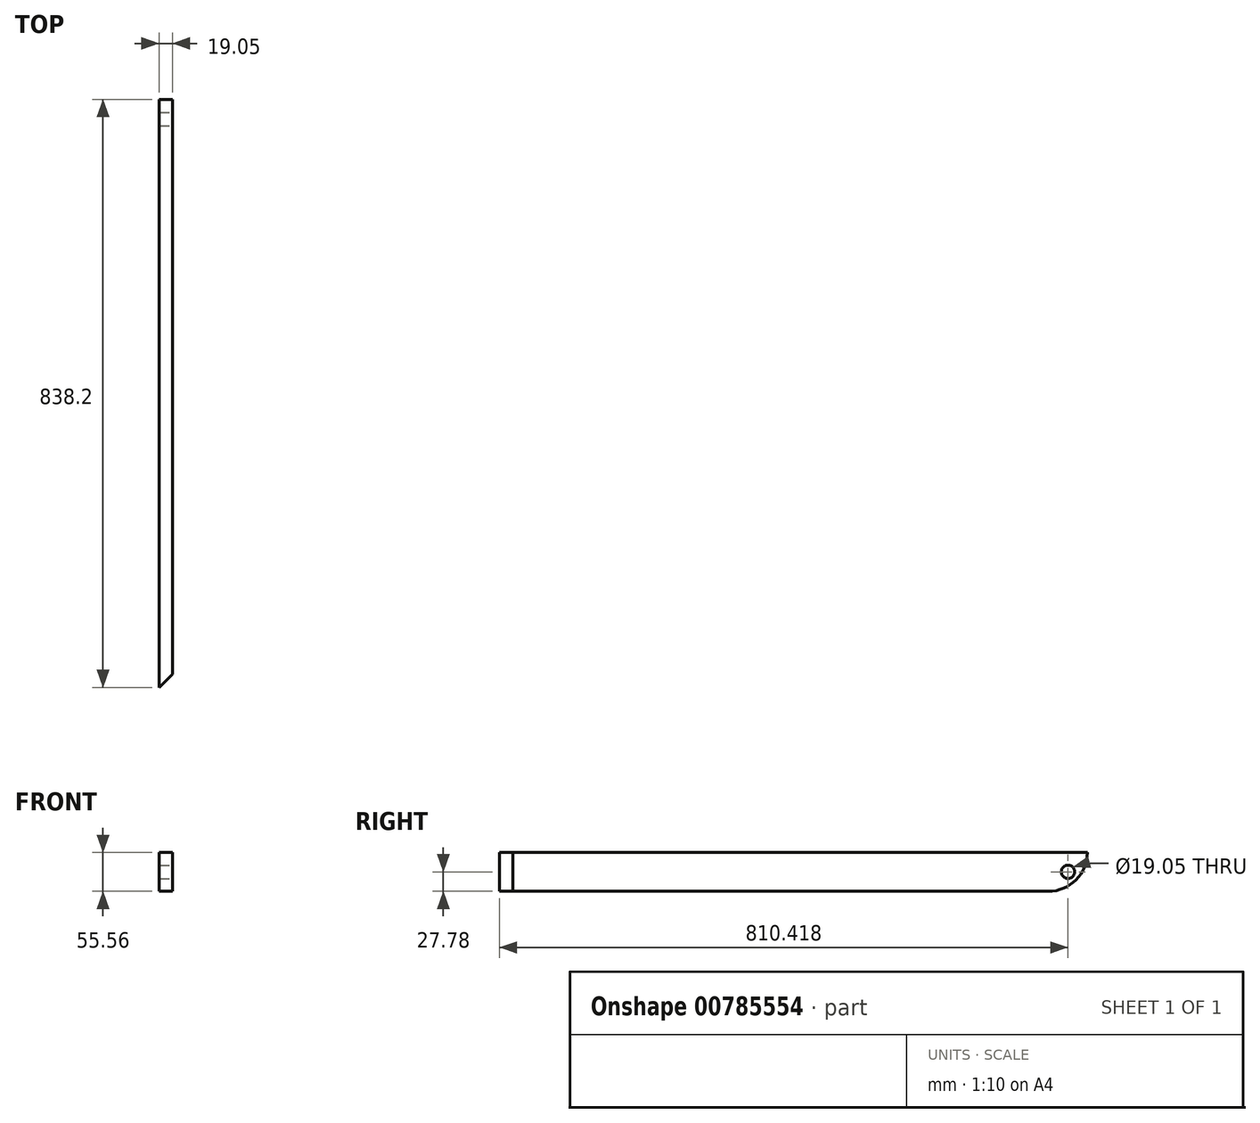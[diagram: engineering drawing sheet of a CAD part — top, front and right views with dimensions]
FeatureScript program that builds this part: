
annotation { "Feature Type Name" : "Feature", "Feature Type Description" : "" }
export const myFeature = defineFeature(function(context is Context, id is Id, definition is map)
    precondition{}
    {
        {
            var Q0;
            Q0=qCreatedBy(makeId("Right.planeOp"),FACE);
            var sketch = newSketch(context, id + "F0", { "sketchPlane" : qUnion([Q0])});
            skLineSegment(sketch, "E0.bottom", {"start": v(428.15, 27.78) * mm, "end": v(-410.05, 27.78) * mm});
            skLineSegment(sketch, "E0.top", {"start": v(428.15, -27.78) * mm, "end": v(-410.05, -27.78) * mm});
            skLineSegment(sketch, "E0.left", {"start": v(428.15, 27.78) * mm, "end": v(428.15, -27.78) * mm});
            skLineSegment(sketch, "E0.right", {"start": v(-410.05, 27.78) * mm, "end": v(-410.05, -27.78) * mm});
            skPoint(sketch, "E0.middle", {"position": v(9.05, 0) * mm});
            skSolve(sketch);
        }
        {
            var Q0;
            Q0 = qSketchRegion(id + "F0", true);
            extrude(context, id + "F1", {"entities" : qUnion([Q0]), "depth" : 19.05 * mm, "offsetDistance" : 25.4 * mm});
        }
        {
            var Q0;
            Q0=makeQuery(id+"F1.opExtrude","SWEPT_EDGE",EDGE,{"disambiguationData":[OSD([sQuery(id+"F0.wireOp",EDGE,"E0.top"),sQuery(id+"F0.wireOp",EDGE,"E0.left")])]});
            fillet(context, id + "F2", {"entities" : qUnion([Q0]), "radius" : 55.56 * mm, "tangentPropagation" : true, "allowEdgeOverflow" : false});
        }
        {
            var Q0;
            Q0=makeQuery(id+"F1.opExtrude","CAP_FACE",FACE,{"disambiguationData":[OSD([sQuery(id+"F0.wireOp",EDGE,"E0.bottom"),sQuery(id+"F0.wireOp",EDGE,"E0.top"),sQuery(id+"F0.wireOp",EDGE,"E0.left"),sQuery(id+"F0.wireOp",EDGE,"E0.right")])],"isStart":false});
            var sketch = newSketch(context, id + "F3", { "sketchPlane" : qUnion([Q0])});
            skCircle(sketch, "E1", {"center": v(400.37, 0) * mm, "radius": 9.53 * mm});
            skPoint(sketch, "E2.orphan", {"position": v(372.59, -27.78) * mm});
            skPoint(sketch, "E3.end.orphan", {"position": v(428.15, 27.78) * mm});
            skSolve(sketch);
        }
        {
            var Q0;
            Q0 = qSketchRegion(id + "F3", true);
            extrude(context, id + "F4", {"entities" : qUnion([Q0]), "operationType" : NewBodyOperationType.REMOVE, "oppositeDirection" : true, "depth" : 25.4 * mm, "offsetDistance" : 25.4 * mm});
        }
        {
            var Q0;
            Q0=makeQuery(id+"F1.opExtrude","SWEPT_FACE",FACE,{"disambiguationData":[OSD([sQuery(id+"F0.wireOp",EDGE,"E0.bottom")])]});
            var sketch = newSketch(context, id + "F5", { "sketchPlane" : qUnion([Q0])});
            skLineSegment(sketch, "E4", {"start": v(0, -410.05) * mm, "end": v(19.05, -391) * mm});
            skSolve(sketch);
        }
        {
            var Q0;
            Q0 = qSketchRegion(id + "F5", true);
            var Q1;
            {var subQ0=sQuery(id+"F5.wireOp",EDGE,"E4");Q1=makeQuery(id+"F5.imprint","IMPRINT",FACE,{"disambiguationData":[TD([[makeQuery(id+"F5.imprint","IMPRINT",EDGE,{"derivedFrom":subQ0}),-1.0]])]});}
            extrude(context, id + "F6", {"entities" : qUnion([Q0, Q1]), "operationType" : NewBodyOperationType.REMOVE, "endBound" : BoundingType.THROUGH_ALL, "oppositeDirection" : true, "depth" : 25.4 * mm, "offsetDistance" : 25.4 * mm});
        }
    });
